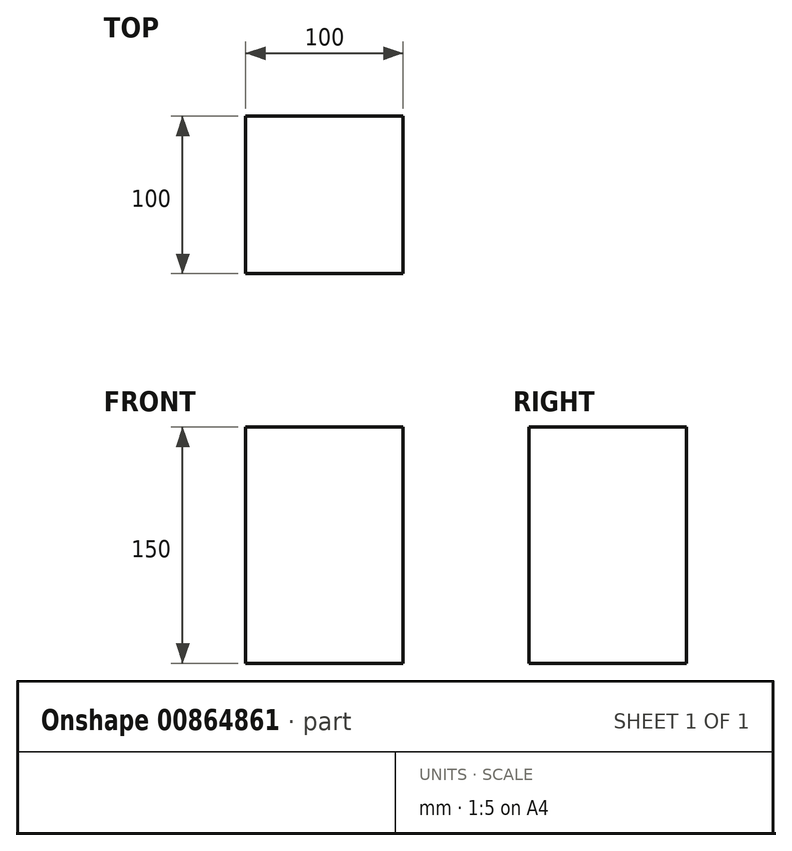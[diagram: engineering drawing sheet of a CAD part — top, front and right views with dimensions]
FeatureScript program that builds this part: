
annotation { "Feature Type Name" : "Feature", "Feature Type Description" : "" }
export const myFeature = defineFeature(function(context is Context, id is Id, definition is map)
    precondition{}
    {
        {
            var Q0;
            Q0=qCreatedBy(makeId("Top.planeOp"),FACE);
            var sketch = newSketch(context, id + "F0", { "sketchPlane" : qUnion([Q0])});
            skLineSegment(sketch, "E0.bottom", {"start": v(183.61, 0) * mm, "end": v(283.61, 0) * mm});
            skLineSegment(sketch, "E0.top", {"start": v(183.61, 100) * mm, "end": v(283.61, 100) * mm});
            skLineSegment(sketch, "E0.left", {"start": v(183.61, 0) * mm, "end": v(183.61, 100) * mm});
            skLineSegment(sketch, "E0.right", {"start": v(283.61, 0) * mm, "end": v(283.61, 100) * mm});
            skSolve(sketch);
        }
        {
            var Q0;
            Q0=makeQuery(id+"F0.imprint","IMPRINT",FACE,{"disambiguationData":[TD([[makeQuery(id+"F0.imprint","IMPRINT",EDGE,{"derivedFrom":sQuery(id+"F0.wireOp",EDGE,"E0.bottom")}),1.0]])]});
            extrude(context, id + "F1", {"entities" : qUnion([Q0]), "depth" : 150 * mm, "offsetDistance" : 25 * mm});
        }
    });
